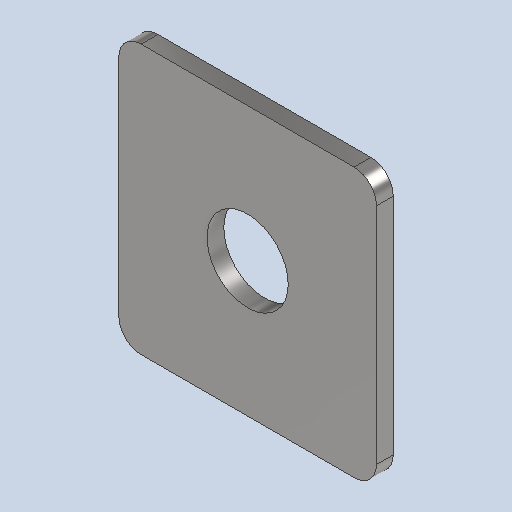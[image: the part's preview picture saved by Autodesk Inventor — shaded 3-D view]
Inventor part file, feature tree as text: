
AUTODESK INVENTOR PART (.ipt)
format: ipt  version: 2025 (Build 290162010, 162A)  size: 142,848 bytes
history: native  units: mm
features: other x2, sheet_metal_op x1, chamfer x1, extrude x1
ambient origin geometry x8: Origin, YZ Plane, XZ Plane, XY Plane, X Axis, Y Axis, Z Axis, Center Point
bodies: Solid1 (feature_tree)
feature tree (5):
  sheet_metal_op  "Face1"
  chamfer  "Corner Round1"
  extrude  "Extrusion1"  Depth=46.0mm
  other  "Plate1"
  other  "Definition1"
